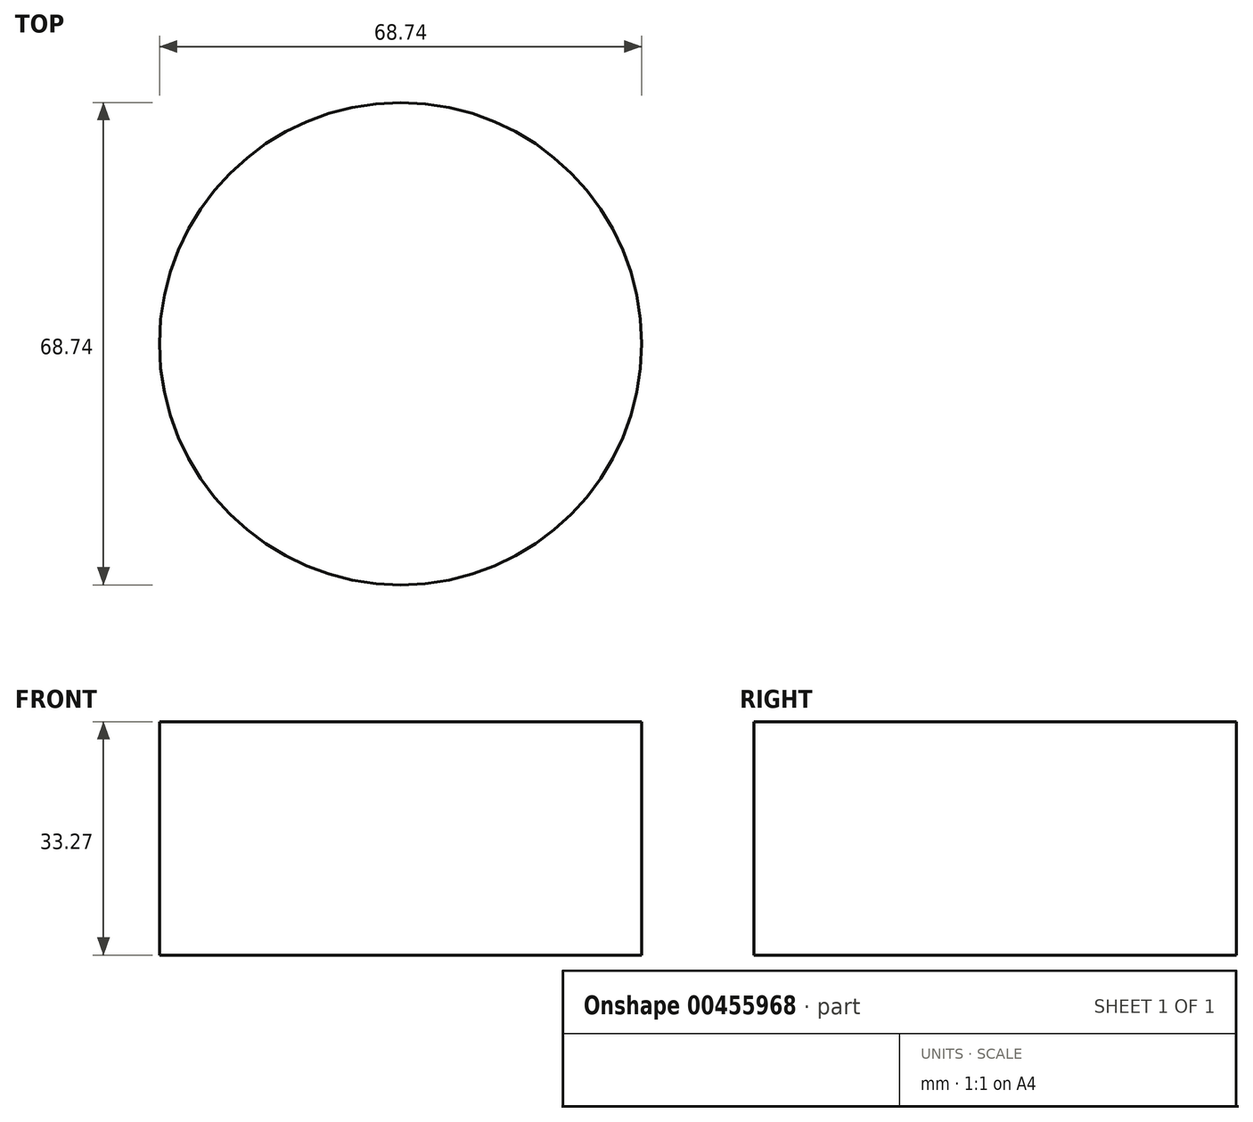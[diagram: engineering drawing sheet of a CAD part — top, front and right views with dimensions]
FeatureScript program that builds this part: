
annotation { "Feature Type Name" : "Feature", "Feature Type Description" : "" }
export const myFeature = defineFeature(function(context is Context, id is Id, definition is map)
    precondition{}
    {
        {
            var Q0;
            Q0=qCreatedBy(makeId("Top.planeOp"),FACE);
            var sketch = newSketch(context, id + "F0", { "sketchPlane" : qUnion([Q0])});
            skCircle(sketch, "E0", {"center": v(0, 0) * mm, "radius": 34.37 * mm});
            skSolve(sketch);
        }
        {
            var Q0;
            Q0=makeQuery(id+"F0.imprint","IMPRINT",FACE,{"disambiguationData":[TD([[makeQuery(id+"F0.imprint","IMPRINT",EDGE,{"derivedFrom":sQuery(id+"F0.wireOp",EDGE,"E0")}),1.0]])]});
            extrude(context, id + "F1", {"entities" : qUnion([Q0]), "depth" : 33.27 * mm});
        }
    });
